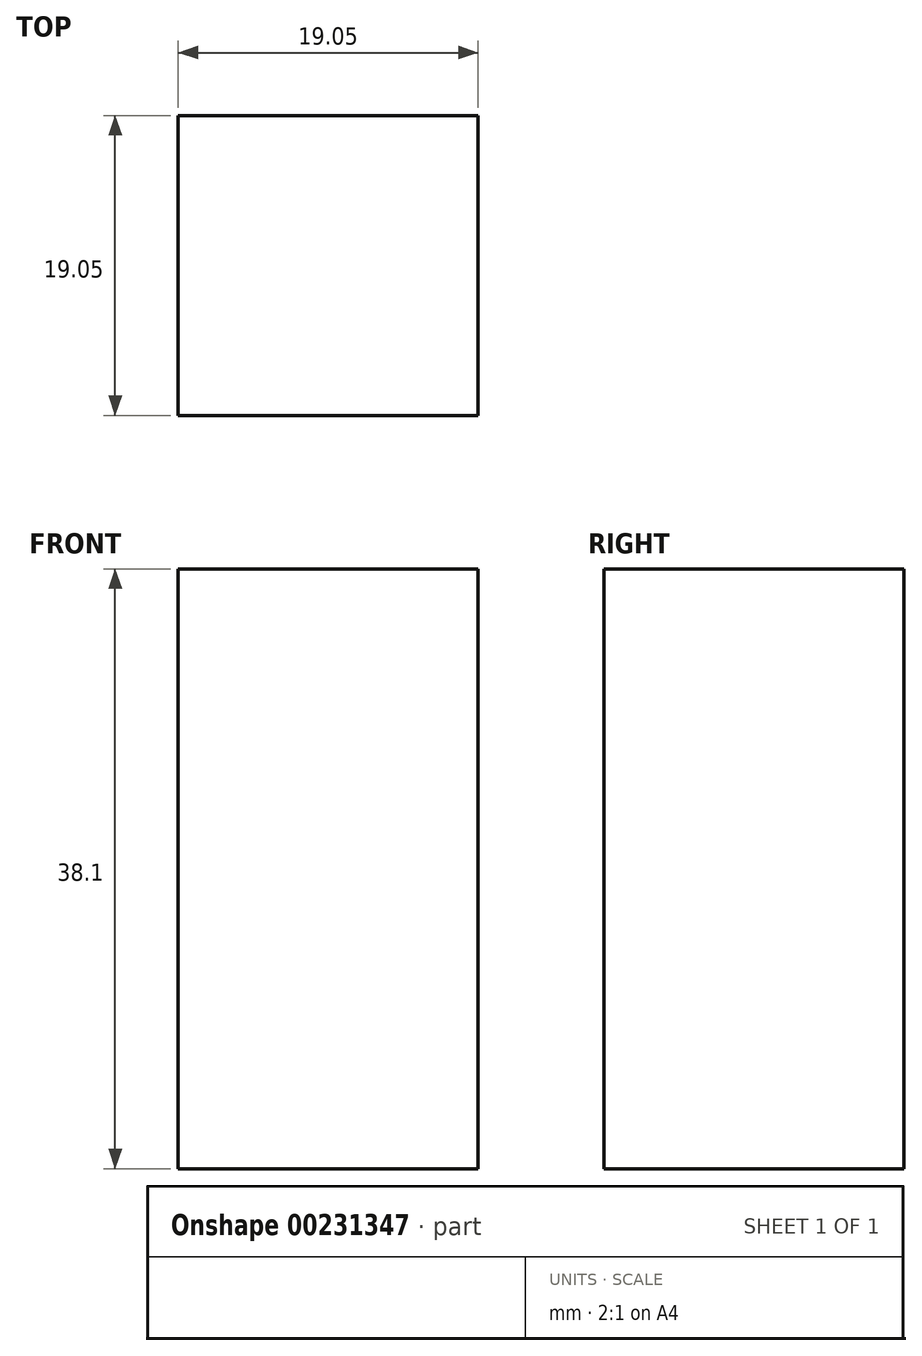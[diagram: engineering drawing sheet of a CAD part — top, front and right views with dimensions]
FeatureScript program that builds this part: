
annotation { "Feature Type Name" : "Feature", "Feature Type Description" : "" }
export const myFeature = defineFeature(function(context is Context, id is Id, definition is map)
    precondition{}
    {
        {
            var Q0;
            Q0=qCreatedBy(makeId("Front.planeOp"),FACE);
            var sketch = newSketch(context, id + "F0", { "sketchPlane" : qUnion([Q0])});
            skLineSegment(sketch, "E0.bottom", {"start": v(-19.05, 38.1) * mm, "end": v(0, 38.1) * mm});
            skLineSegment(sketch, "E0.top", {"start": v(-19.05, 0) * mm, "end": v(0, 0) * mm});
            skLineSegment(sketch, "E0.left", {"start": v(-19.05, 38.1) * mm, "end": v(-19.05, 0) * mm});
            skLineSegment(sketch, "E0.right", {"start": v(0, 38.1) * mm, "end": v(0, 0) * mm});
            skSolve(sketch);
        }
        {
            var Q0;
            Q0 = qSketchRegion(id + "F0", true);
            extrude(context, id + "F1", {"entities" : qUnion([Q0]), "depth" : 19.05 * mm});
        }
    });
